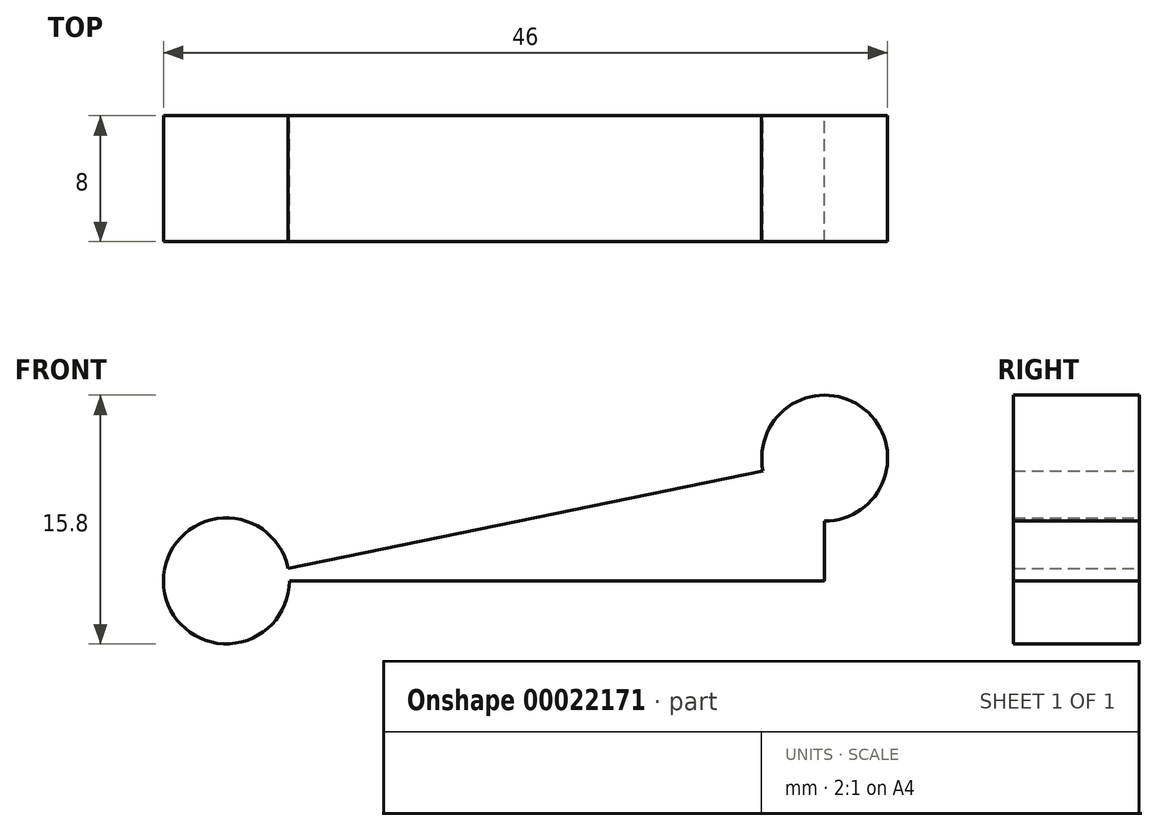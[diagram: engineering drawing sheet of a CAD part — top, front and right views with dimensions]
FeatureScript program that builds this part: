
annotation { "Feature Type Name" : "Feature", "Feature Type Description" : "" }
export const myFeature = defineFeature(function(context is Context, id is Id, definition is map)
    precondition{}
    {
        {
            var Q0;
            Q0=qCreatedBy(makeId("Front.planeOp"),FACE);
            var sketch = newSketch(context, id + "F0", { "sketchPlane" : qUnion([Q0])});
            skLineSegment(sketch, "E0", {"start": v(0, 0) * mm, "end": v(0, 7.8) * mm});
            skLineSegment(sketch, "E1", {"start": v(0, 7.8) * mm, "end": v(-38, 0) * mm});
            skLineSegment(sketch, "E2", {"start": v(-38, 0) * mm, "end": v(0, 0) * mm});
            skCircle(sketch, "E3", {"center": v(-38, 0) * mm, "radius": 4 * mm});
            skCircle(sketch, "E4", {"center": v(0, 7.8) * mm, "radius": 4 * mm});
            skSolve(sketch);
        }
        {
            var Q0;
            Q0 = qSketchRegion(id + "F0", true);
            extrude(context, id + "F1", {"entities" : qUnion([Q0]), "depth" : 8 * mm});
        }
    });
